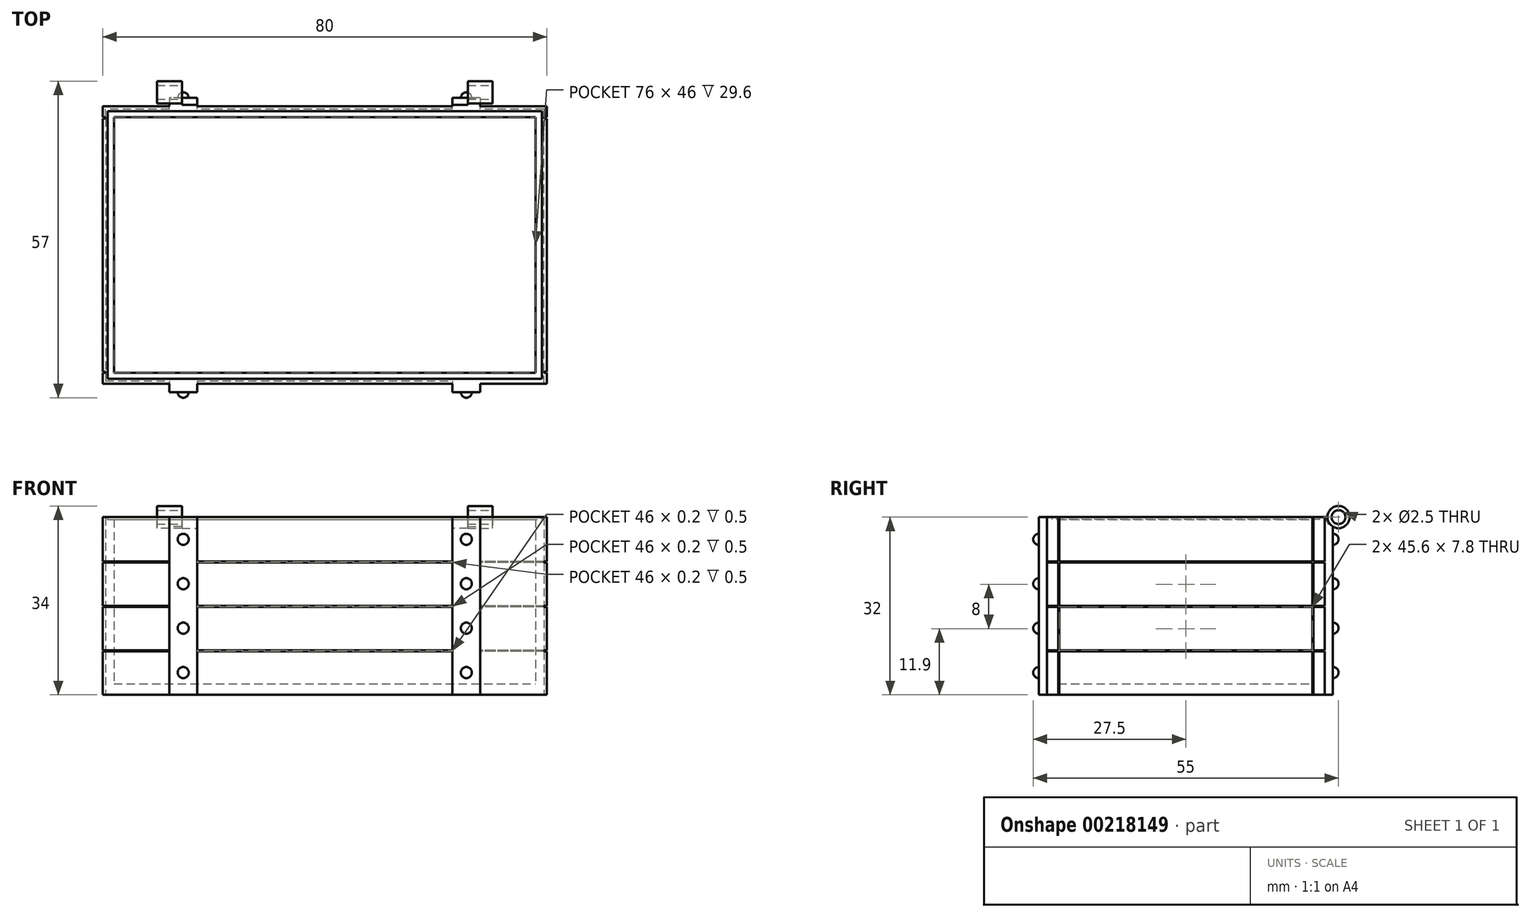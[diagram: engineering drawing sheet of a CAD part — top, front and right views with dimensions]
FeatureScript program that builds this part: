
annotation { "Feature Type Name" : "Feature", "Feature Type Description" : "" }
export const myFeature = defineFeature(function(context is Context, id is Id, definition is map)
    precondition{}
    {
        {
            var Q0;
            Q0=qCreatedBy(makeId("Top.planeOp"),FACE);
            var sketch = newSketch(context, id + "F0", { "sketchPlane" : qUnion([Q0])});
            skLineSegment(sketch, "E0.bottom", {"start": v(40, -25) * mm, "end": v(-40, -25) * mm});
            skLineSegment(sketch, "E0.top", {"start": v(40, 25) * mm, "end": v(-40, 25) * mm});
            skLineSegment(sketch, "E0.left", {"start": v(40, -25) * mm, "end": v(40, 25) * mm});
            skLineSegment(sketch, "E0.right", {"start": v(-40, -25) * mm, "end": v(-40, 25) * mm});
            skPoint(sketch, "E0.middle", {"position": v(0, 0) * mm});
            skSolve(sketch);
        }
        {
            var Q0;
            Q0 = qSketchRegion(id + "F0", true);
            extrude(context, id + "F1", {"entities" : qUnion([Q0]), "depth" : 2 * mm});
        }
        {
            var Q0;
            Q0=makeQuery(id+"F1.opExtrude","CAP_FACE",FACE,{"disambiguationData":[OSD([sQuery(id+"F0.wireOp",EDGE,"E0.bottom"),sQuery(id+"F0.wireOp",EDGE,"E0.top"),sQuery(id+"F0.wireOp",EDGE,"E0.left"),sQuery(id+"F0.wireOp",EDGE,"E0.right")])],"isStart":false});
            var sketch = newSketch(context, id + "F2", { "sketchPlane" : qUnion([Q0])});
            skLineSegment(sketch, "E1.bottom", {"start": v(40, -25) * mm, "end": v(-40, -25) * mm});
            skLineSegment(sketch, "E1.top", {"start": v(40, 25) * mm, "end": v(-40, 25) * mm});
            skLineSegment(sketch, "E1.left", {"start": v(40, -25) * mm, "end": v(40, 25) * mm});
            skLineSegment(sketch, "E1.right", {"start": v(-40, -25) * mm, "end": v(-40, 25) * mm});
            skPoint(sketch, "E1.middle", {"position": v(0, 0) * mm});
            skLineSegment(sketch, "E2.0", {"start": v(38, -23) * mm, "end": v(38, 23) * mm});
            skLineSegment(sketch, "E2.1", {"start": v(-38, -23) * mm, "end": v(38, -23) * mm});
            skLineSegment(sketch, "E2.2", {"start": v(-38, 23) * mm, "end": v(-38, -23) * mm});
            skLineSegment(sketch, "E2.3", {"start": v(38, 23) * mm, "end": v(-38, 23) * mm});
            skSolve(sketch);
        }
        {
            var Q0;
            Q0 = qSketchRegion(id + "F2", true);
            extrude(context, id + "F3", {"entities" : qUnion([Q0]), "operationType" : NewBodyOperationType.ADD, "depth" : 30 * mm});
        }
        {
            var Q0;
            Q0=makeQuery(id+"F3.boolean.opBoolean","MERGE",FACE,{"derivedFrom":[makeQuery(id+"F1.opExtrude","SWEPT_FACE",FACE,{"disambiguationData":[OSD([sQuery(id+"F0.wireOp",EDGE,"E0.top")])]}),makeQuery(id+"F3.opExtrude","SWEPT_FACE",FACE,{"disambiguationData":[OSD([sQuery(id+"F2.wireOp",EDGE,"E1.top")])]})]});
            var sketch = newSketch(context, id + "F4", { "sketchPlane" : qUnion([Q0])});
            skLineSegment(sketch, "E3.bottom", {"start": v(-28, 32) * mm, "end": v(-23, 32) * mm});
            skLineSegment(sketch, "E3.top", {"start": v(-28, 0) * mm, "end": v(-23, 0) * mm});
            skLineSegment(sketch, "E3.left", {"start": v(-28, 32) * mm, "end": v(-28, 0) * mm});
            skLineSegment(sketch, "E3.right", {"start": v(-23, 32) * mm, "end": v(-23, 0) * mm});
            skLineSegment(sketch, "E4.MirrorCS", {"start": v(23, 32) * mm, "end": v(23, 0) * mm});
            skLineSegment(sketch, "E5.MirrorCS", {"start": v(28, 32) * mm, "end": v(23, 32) * mm});
            skLineSegment(sketch, "E6.MirrorCS", {"start": v(28, 32) * mm, "end": v(28, 0) * mm});
            skLineSegment(sketch, "E7.MirrorCS", {"start": v(28, 0) * mm, "end": v(23, 0) * mm});
            skSolve(sketch);
        }
        {
            var Q0;
            Q0 = qSketchRegion(id + "F4", true);
            extrude(context, id + "F5", {"entities" : qUnion([Q0]), "operationType" : NewBodyOperationType.ADD, "depth" : 1.5 * mm});
        }
        {
            var Q0;
            Q0=makeQuery(id+"F5.opExtrude","SWEPT_FACE",FACE,{"disambiguationData":[OSD([sQuery(id+"F4.wireOp",EDGE,"E3.left")])]});
            var sketch = newSketch(context, id + "F6", { "sketchPlane" : qUnion([Q0])});
            skCircle(sketch, "E8", {"center": v(27.5, 32) * mm, "radius": 2 * mm});
            skSolve(sketch);
        }
        {
            var Q0;
            Q0 = qSketchRegion(id + "F6", true);
            extrude(context, id + "F7", {"entities" : qUnion([Q0]), "operationType" : NewBodyOperationType.ADD, "oppositeDirection" : true, "depth" : 4.5 * mm, "symmetric" : true});
        }
        {
            var Q0;
            Q0=makeQuery(id+"F5.opExtrude","SWEPT_FACE",FACE,{"disambiguationData":[OSD([sQuery(id+"F4.wireOp",EDGE,"E6.MirrorCS")])]});
            var sketch = newSketch(context, id + "F8", { "sketchPlane" : qUnion([Q0])});
            skCircle(sketch, "E9", {"center": v(-27.5, 32) * mm, "radius": 2 * mm});
            skSolve(sketch);
        }
        {
            var Q0;
            Q0 = qSketchRegion(id + "F8", true);
            extrude(context, id + "F9", {"entities" : qUnion([Q0]), "operationType" : NewBodyOperationType.ADD, "oppositeDirection" : true, "depth" : 4.5 * mm, "symmetric" : true});
        }
        {
            var Q0;
            Q0=qCreatedBy(makeId("Right.planeOp"),FACE);
            var sketch = newSketch(context, id + "F10", { "sketchPlane" : qUnion([Q0])});
            skCircle(sketch, "E10", {"center": v(27.5, 32) * mm, "radius": 1.25 * mm});
            skSolve(sketch);
        }
        {
            var Q0;
            Q0 = qSketchRegion(id + "F10", true);
            extrude(context, id + "F11", {"entities" : qUnion([Q0]), "operationType" : NewBodyOperationType.REMOVE, "oppositeDirection" : true, "depth" : 70 * mm, "symmetric" : true});
        }
        {
            var Q0;
            Q0=makeQuery(id+"F3.boolean.opBoolean","MERGE",FACE,{"derivedFrom":[makeQuery(id+"F1.opExtrude","SWEPT_FACE",FACE,{"disambiguationData":[OSD([sQuery(id+"F0.wireOp",EDGE,"E0.bottom")])]}),makeQuery(id+"F3.opExtrude","SWEPT_FACE",FACE,{"disambiguationData":[OSD([sQuery(id+"F2.wireOp",EDGE,"E1.bottom")])]})]});
            var sketch = newSketch(context, id + "F12", { "sketchPlane" : qUnion([Q0])});
            skLineSegment(sketch, "E11.bottom", {"start": v(-28, 0) * mm, "end": v(-23, 0) * mm});
            skLineSegment(sketch, "E11.top", {"start": v(-28, 32) * mm, "end": v(-23, 32) * mm});
            skLineSegment(sketch, "E11.left", {"start": v(-28, 0) * mm, "end": v(-28, 32) * mm});
            skLineSegment(sketch, "E11.right", {"start": v(-23, 0) * mm, "end": v(-23, 32) * mm});
            skLineSegment(sketch, "E12.bottom", {"start": v(23, 0) * mm, "end": v(28, 0) * mm});
            skLineSegment(sketch, "E12.top", {"start": v(23, 32) * mm, "end": v(28, 32) * mm});
            skLineSegment(sketch, "E12.left", {"start": v(23, 0) * mm, "end": v(23, 32) * mm});
            skLineSegment(sketch, "E12.right", {"start": v(28, 0) * mm, "end": v(28, 32) * mm});
            skSolve(sketch);
        }
        {
            var Q0;
            Q0 = qSketchRegion(id + "F12", true);
            extrude(context, id + "F13", {"entities" : qUnion([Q0]), "operationType" : NewBodyOperationType.ADD, "depth" : 1.5 * mm});
        }
        {
            var Q0;
            Q0=makeQuery(id+"F5.opExtrude","SWEPT_FACE",FACE,{"disambiguationData":[OSD([sQuery(id+"F4.wireOp",EDGE,"E4.MirrorCS")])]});
            var sketch = newSketch(context, id + "F14", { "sketchPlane" : qUnion([Q0])});
            skCircle(sketch, "E13", {"center": v(27.5, 32) * mm, "radius": 2.25 * mm});
            skSolve(sketch);
        }
        {
            var Q0;
            {var subQ1=sQuery(id+"F4.wireOp",EDGE,"E4.MirrorCS");var subQ6=makeQuery(id+"F11.boolean.opBoolean","INTERSECT",EDGE,{"derivedFrom":[makeQuery(id+"F5.opExtrude","SWEPT_FACE",FACE,{"disambiguationData":[OSD([subQ1])]}),makeQuery(id+"F11.opExtrude","SWEPT_FACE",FACE,{"disambiguationData":[OSD([sQuery(id+"F10.wireOp",EDGE,"E10")])]})]});Q0=makeQuery(id+"F14.imprint","IMPRINT",FACE,{"disambiguationData":[TD([[makeQuery(id+"F14.imprint","IMPRINT",EDGE,{"derivedFrom":subQ6}),1.0]])]});}
            var Q1;
            Q1=makeQuery(id+"F9.opExtrude","CAP_FACE",FACE,{"disambiguationData":[OSD([sQuery(id+"F8.wireOp",EDGE,"E9")])],"isStart":false});
            extrude(context, id + "F15", {"entities" : qUnion([Q0]), "operationType" : NewBodyOperationType.REMOVE, "endBound" : BoundingType.UP_TO_SURFACE, "oppositeDirection" : true, "endBoundEntityFace" : qUnion([Q1]), "depth" : 25 * mm});
        }
        {
            var Q0;
            Q0=makeQuery(id+"F5.opExtrude","SWEPT_FACE",FACE,{"disambiguationData":[OSD([sQuery(id+"F4.wireOp",EDGE,"E3.right")])]});
            var sketch = newSketch(context, id + "F16", { "sketchPlane" : qUnion([Q0])});
            skCircle(sketch, "E14", {"center": v(-27.5, 32) * mm, "radius": 2.25 * mm});
            skSolve(sketch);
        }
        {
            var Q0;
            {var subQ1=sQuery(id+"F4.wireOp",EDGE,"E3.right");var subQ6=makeQuery(id+"F11.boolean.opBoolean","INTERSECT",EDGE,{"derivedFrom":[makeQuery(id+"F5.opExtrude","SWEPT_FACE",FACE,{"disambiguationData":[OSD([subQ1])]}),makeQuery(id+"F11.opExtrude","SWEPT_FACE",FACE,{"disambiguationData":[OSD([sQuery(id+"F10.wireOp",EDGE,"E10")])]})]});Q0=makeQuery(id+"F16.imprint","IMPRINT",FACE,{"disambiguationData":[TD([[makeQuery(id+"F16.imprint","IMPRINT",EDGE,{"derivedFrom":subQ6}),-1.0]])]});}
            var Q1;
            Q1=makeQuery(id+"F7.opExtrude","CAP_FACE",FACE,{"disambiguationData":[OSD([sQuery(id+"F6.wireOp",EDGE,"E8")])],"isStart":false});
            extrude(context, id + "F17", {"entities" : qUnion([Q0]), "operationType" : NewBodyOperationType.REMOVE, "endBound" : BoundingType.UP_TO_SURFACE, "oppositeDirection" : true, "endBoundEntityFace" : qUnion([Q1]), "depth" : 25 * mm});
        }
        {
            var Q0;
            Q0=makeQuery(id+"F13.opExtrude","CAP_FACE",FACE,{"disambiguationData":[OSD([sQuery(id+"F12.wireOp",EDGE,"E11.bottom"),sQuery(id+"F12.wireOp",EDGE,"E11.top"),sQuery(id+"F12.wireOp",EDGE,"E11.left"),sQuery(id+"F12.wireOp",EDGE,"E11.right")])],"isStart":false});
            var sketch = newSketch(context, id + "F18", { "sketchPlane" : qUnion([Q0])});
            skLineSegment(sketch, "E15", {"start": v(-25.5, 32) * mm, "end": v(-25.5, 0) * mm, "construction": true});
            skCircle(sketch, "E16", {"center": v(-25.5, 28) * mm, "radius": 1 * mm});
            skCircle(sketch, "E17", {"center": v(-25.5, 20) * mm, "radius": 1 * mm});
            skCircle(sketch, "E18", {"center": v(-25.5, 12) * mm, "radius": 1 * mm});
            skCircle(sketch, "E19", {"center": v(-25.5, 4) * mm, "radius": 1 * mm});
            skSolve(sketch);
        }
        {
            var Q0;
            Q0=makeQuery(id+"F13.opExtrude","CAP_FACE",FACE,{"disambiguationData":[OSD([sQuery(id+"F12.wireOp",EDGE,"E12.bottom"),sQuery(id+"F12.wireOp",EDGE,"E12.top"),sQuery(id+"F12.wireOp",EDGE,"E12.left"),sQuery(id+"F12.wireOp",EDGE,"E12.right")])],"isStart":false});
            var sketch = newSketch(context, id + "F19", { "sketchPlane" : qUnion([Q0])});
            skLineSegment(sketch, "E20", {"start": v(25.5, 32) * mm, "end": v(25.5, 0) * mm, "construction": true});
            skCircle(sketch, "E21", {"center": v(25.5, 28) * mm, "radius": 1 * mm});
            skCircle(sketch, "E22", {"center": v(25.5, 20) * mm, "radius": 1 * mm});
            skCircle(sketch, "E23", {"center": v(25.5, 12) * mm, "radius": 1 * mm});
            skCircle(sketch, "E24", {"center": v(25.5, 4) * mm, "radius": 1 * mm});
            skSolve(sketch);
        }
        {
            var Q0;
            Q0=makeQuery(id+"F18.imprint","IMPRINT",FACE,{"disambiguationData":[TD([[makeQuery(id+"F18.imprint","IMPRINT",EDGE,{"derivedFrom":sQuery(id+"F18.wireOp",EDGE,"E16")}),1.0]])]});
            var Q1;
            Q1=makeQuery(id+"F18.imprint","IMPRINT",FACE,{"disambiguationData":[TD([[makeQuery(id+"F18.imprint","IMPRINT",EDGE,{"derivedFrom":sQuery(id+"F18.wireOp",EDGE,"E17")}),1.0]])]});
            var Q2;
            Q2=makeQuery(id+"F18.imprint","IMPRINT",FACE,{"disambiguationData":[TD([[makeQuery(id+"F18.imprint","IMPRINT",EDGE,{"derivedFrom":sQuery(id+"F18.wireOp",EDGE,"E18")}),1.0]])]});
            var Q3;
            Q3=makeQuery(id+"F18.imprint","IMPRINT",FACE,{"disambiguationData":[TD([[makeQuery(id+"F18.imprint","IMPRINT",EDGE,{"derivedFrom":sQuery(id+"F18.wireOp",EDGE,"E19")}),1.0]])]});
            var Q4;
            Q4=makeQuery(id+"F19.imprint","IMPRINT",FACE,{"disambiguationData":[TD([[makeQuery(id+"F19.imprint","IMPRINT",EDGE,{"derivedFrom":sQuery(id+"F19.wireOp",EDGE,"E21")}),1.0]])]});
            var Q5;
            Q5=makeQuery(id+"F19.imprint","IMPRINT",FACE,{"disambiguationData":[TD([[makeQuery(id+"F19.imprint","IMPRINT",EDGE,{"derivedFrom":sQuery(id+"F19.wireOp",EDGE,"E22")}),1.0]])]});
            var Q6;
            Q6=makeQuery(id+"F19.imprint","IMPRINT",FACE,{"disambiguationData":[TD([[makeQuery(id+"F19.imprint","IMPRINT",EDGE,{"derivedFrom":sQuery(id+"F19.wireOp",EDGE,"E23")}),1.0]])]});
            var Q7;
            Q7=makeQuery(id+"F19.imprint","IMPRINT",FACE,{"disambiguationData":[TD([[makeQuery(id+"F19.imprint","IMPRINT",EDGE,{"derivedFrom":sQuery(id+"F19.wireOp",EDGE,"E24")}),1.0]])]});
            extrude(context, id + "F20", {"entities" : qUnion([Q0, Q1, Q2, Q3, Q4, Q5, Q6, Q7]), "operationType" : NewBodyOperationType.ADD, "depth" : 1 * mm});
        }
        {
            var Q0;
            Q0=makeQuery(id+"F20.opExtrude","CAP_FACE",FACE,{"disambiguationData":[OSD([sQuery(id+"F18.wireOp",EDGE,"E16")])],"isStart":false});
            var Q1;
            Q1=makeQuery(id+"F20.opExtrude","CAP_FACE",FACE,{"disambiguationData":[OSD([sQuery(id+"F18.wireOp",EDGE,"E17")])],"isStart":false});
            var Q2;
            Q2=makeQuery(id+"F20.opExtrude","CAP_FACE",FACE,{"disambiguationData":[OSD([sQuery(id+"F18.wireOp",EDGE,"E18")])],"isStart":false});
            var Q3;
            Q3=makeQuery(id+"F20.opExtrude","CAP_FACE",FACE,{"disambiguationData":[OSD([sQuery(id+"F18.wireOp",EDGE,"E19")])],"isStart":false});
            var Q4;
            Q4=makeQuery(id+"F20.opExtrude","CAP_FACE",FACE,{"disambiguationData":[OSD([sQuery(id+"F19.wireOp",EDGE,"E21")])],"isStart":false});
            var Q5;
            Q5=makeQuery(id+"F20.opExtrude","CAP_FACE",FACE,{"disambiguationData":[OSD([sQuery(id+"F19.wireOp",EDGE,"E22")])],"isStart":false});
            var Q6;
            Q6=makeQuery(id+"F20.opExtrude","CAP_FACE",FACE,{"disambiguationData":[OSD([sQuery(id+"F19.wireOp",EDGE,"E23")])],"isStart":false});
            var Q7;
            Q7=makeQuery(id+"F20.opExtrude","CAP_EDGE",EDGE,{"disambiguationData":[OSD([sQuery(id+"F19.wireOp",EDGE,"E24")])],"isStart":false});
            fillet(context, id + "F21", {"entities" : qUnion([Q0, Q1, Q2, Q3, Q4, Q5, Q6, Q7]), "radius" : 1 * mm, "tangentPropagation" : true, "allowEdgeOverflow" : false});
        }
        {
            var Q0;
            Q0=makeQuery(id+"F5.opExtrude","CAP_FACE",FACE,{"disambiguationData":[OSD([sQuery(id+"F4.wireOp",EDGE,"E3.bottom"),sQuery(id+"F4.wireOp",EDGE,"E3.top"),sQuery(id+"F4.wireOp",EDGE,"E3.left"),sQuery(id+"F4.wireOp",EDGE,"E3.right")])],"isStart":false});
            var sketch = newSketch(context, id + "F22", { "sketchPlane" : qUnion([Q0])});
            skLineSegment(sketch, "E25", {"start": v(-25.5, 0) * mm, "end": v(-25.5, 29.98) * mm, "construction": true});
            skCircle(sketch, "E26", {"center": v(-25.5, 4) * mm, "radius": 1 * mm});
            skCircle(sketch, "E27", {"center": v(-25.5, 12) * mm, "radius": 1 * mm});
            skCircle(sketch, "E28", {"center": v(-25.5, 20) * mm, "radius": 1 * mm});
            skCircle(sketch, "E29", {"center": v(-25.5, 28) * mm, "radius": 1 * mm});
            skSolve(sketch);
        }
        {
            var Q0;
            Q0=makeQuery(id+"F5.opExtrude","CAP_FACE",FACE,{"disambiguationData":[OSD([sQuery(id+"F4.wireOp",EDGE,"E4.MirrorCS"),sQuery(id+"F4.wireOp",EDGE,"E5.MirrorCS"),sQuery(id+"F4.wireOp",EDGE,"E6.MirrorCS"),sQuery(id+"F4.wireOp",EDGE,"E7.MirrorCS")])],"isStart":false});
            var sketch = newSketch(context, id + "F23", { "sketchPlane" : qUnion([Q0])});
            skLineSegment(sketch, "E30", {"start": v(25.5, 0) * mm, "end": v(25.5, 29.98) * mm, "construction": true});
            skCircle(sketch, "E31", {"center": v(25.5, 4) * mm, "radius": 1 * mm});
            skCircle(sketch, "E32", {"center": v(25.5, 12) * mm, "radius": 1 * mm});
            skCircle(sketch, "E33", {"center": v(25.5, 20) * mm, "radius": 1 * mm});
            skCircle(sketch, "E34", {"center": v(25.5, 28) * mm, "radius": 1 * mm});
            skSolve(sketch);
        }
        {
            var Q0;
            Q0=makeQuery(id+"F22.imprint","IMPRINT",FACE,{"disambiguationData":[TD([[makeQuery(id+"F22.imprint","IMPRINT",EDGE,{"derivedFrom":sQuery(id+"F22.wireOp",EDGE,"E29")}),1.0]])]});
            var Q1;
            Q1=makeQuery(id+"F22.imprint","IMPRINT",FACE,{"disambiguationData":[TD([[makeQuery(id+"F22.imprint","IMPRINT",EDGE,{"derivedFrom":sQuery(id+"F22.wireOp",EDGE,"E28")}),1.0]])]});
            var Q2;
            Q2=makeQuery(id+"F22.imprint","IMPRINT",FACE,{"disambiguationData":[TD([[makeQuery(id+"F22.imprint","IMPRINT",EDGE,{"derivedFrom":sQuery(id+"F22.wireOp",EDGE,"E27")}),1.0]])]});
            var Q3;
            Q3=makeQuery(id+"F22.imprint","IMPRINT",FACE,{"disambiguationData":[TD([[makeQuery(id+"F22.imprint","IMPRINT",EDGE,{"derivedFrom":sQuery(id+"F22.wireOp",EDGE,"E26")}),1.0]])]});
            var Q4;
            Q4=makeQuery(id+"F23.imprint","IMPRINT",FACE,{"disambiguationData":[TD([[makeQuery(id+"F23.imprint","IMPRINT",EDGE,{"derivedFrom":sQuery(id+"F23.wireOp",EDGE,"E34")}),1.0]])]});
            var Q5;
            Q5=makeQuery(id+"F23.imprint","IMPRINT",FACE,{"disambiguationData":[TD([[makeQuery(id+"F23.imprint","IMPRINT",EDGE,{"derivedFrom":sQuery(id+"F23.wireOp",EDGE,"E33")}),1.0]])]});
            var Q6;
            Q6=makeQuery(id+"F23.imprint","IMPRINT",FACE,{"disambiguationData":[TD([[makeQuery(id+"F23.imprint","IMPRINT",EDGE,{"derivedFrom":sQuery(id+"F23.wireOp",EDGE,"E32")}),1.0]])]});
            var Q7;
            Q7=makeQuery(id+"F23.imprint","IMPRINT",FACE,{"disambiguationData":[TD([[makeQuery(id+"F23.imprint","IMPRINT",EDGE,{"derivedFrom":sQuery(id+"F23.wireOp",EDGE,"E31")}),1.0]])]});
            extrude(context, id + "F24", {"entities" : qUnion([Q0, Q1, Q2, Q3, Q4, Q5, Q6, Q7]), "operationType" : NewBodyOperationType.ADD, "depth" : 1 * mm});
        }
        {
            var Q0;
            Q0=makeQuery(id+"F24.opExtrude","CAP_FACE",FACE,{"disambiguationData":[OSD([sQuery(id+"F22.wireOp",EDGE,"E29")])],"isStart":false});
            var Q1;
            Q1=makeQuery(id+"F24.opExtrude","CAP_EDGE",EDGE,{"disambiguationData":[OSD([sQuery(id+"F22.wireOp",EDGE,"E28")])],"isStart":false});
            var Q2;
            Q2=makeQuery(id+"F24.opExtrude","CAP_EDGE",EDGE,{"disambiguationData":[OSD([sQuery(id+"F22.wireOp",EDGE,"E27")])],"isStart":false});
            var Q3;
            Q3=makeQuery(id+"F24.opExtrude","CAP_EDGE",EDGE,{"disambiguationData":[OSD([sQuery(id+"F22.wireOp",EDGE,"E26")])],"isStart":false});
            var Q4;
            Q4=makeQuery(id+"F24.opExtrude","CAP_FACE",FACE,{"disambiguationData":[OSD([sQuery(id+"F23.wireOp",EDGE,"E34")])],"isStart":false});
            var Q5;
            Q5=makeQuery(id+"F24.opExtrude","CAP_FACE",FACE,{"disambiguationData":[OSD([sQuery(id+"F23.wireOp",EDGE,"E33")])],"isStart":false});
            var Q6;
            Q6=makeQuery(id+"F24.opExtrude","CAP_EDGE",EDGE,{"disambiguationData":[OSD([sQuery(id+"F23.wireOp",EDGE,"E32")])],"isStart":false});
            var Q7;
            Q7=makeQuery(id+"F24.opExtrude","CAP_EDGE",EDGE,{"disambiguationData":[OSD([sQuery(id+"F23.wireOp",EDGE,"E31")])],"isStart":false});
            fillet(context, id + "F25", {"entities" : qUnion([Q0, Q1, Q2, Q3, Q4, Q5, Q6, Q7]), "radius" : 1 * mm, "tangentPropagation" : true, "allowEdgeOverflow" : false});
        }
        {
            var Q0;
            {var subQ0=sQuery(id+"F0.wireOp",EDGE,"E0.bottom");var subQ1=sQuery(id+"F2.wireOp",EDGE,"E1.bottom");Q0=makeQuery(id+"F13.boolean.opBoolean","SPLIT",FACE,{"disambiguationData":[TD([makeQuery(id+"F13.opExtrude","SWEPT_FACE",FACE,{"disambiguationData":[OSD([sQuery(id+"F12.wireOp",EDGE,"E11.right")])]})])],"derivedFrom":makeQuery(id+"F3.boolean.opBoolean","MERGE",FACE,{"derivedFrom":[makeQuery(id+"F1.opExtrude","SWEPT_FACE",FACE,{"disambiguationData":[OSD([subQ0])]}),makeQuery(id+"F3.opExtrude","SWEPT_FACE",FACE,{"disambiguationData":[OSD([subQ1])]})]})});}
            var sketch = newSketch(context, id + "F26", { "sketchPlane" : qUnion([Q0])});
            skLineSegment(sketch, "E35.bottom", {"start": v(-40, 0) * mm, "end": v(40, 0) * mm});
            skLineSegment(sketch, "E35.top", {"start": v(-40, 32) * mm, "end": v(40, 32) * mm});
            skLineSegment(sketch, "E35.left", {"start": v(-40, 0) * mm, "end": v(-40, 32) * mm});
            skLineSegment(sketch, "E35.right", {"start": v(40, 0) * mm, "end": v(40, 32) * mm});
            skLineSegment(sketch, "E36", {"start": v(-40, 24) * mm, "end": v(-28, 24) * mm});
            skLineSegment(sketch, "E37", {"start": v(-40, 16) * mm, "end": v(-28, 16) * mm});
            skLineSegment(sketch, "E38", {"start": v(-40, 8) * mm, "end": v(-28, 8) * mm});
            skLineSegment(sketch, "E39", {"start": v(-40, 23.8) * mm, "end": v(-28, 23.8) * mm});
            skLineSegment(sketch, "E40", {"start": v(-40, 15.8) * mm, "end": v(-28, 15.8) * mm});
            skLineSegment(sketch, "E41", {"start": v(-40, 7.8) * mm, "end": v(-28, 7.8) * mm});
            skLineSegment(sketch, "E42", {"start": v(-40, 24) * mm, "end": v(-40, 23.8) * mm});
            skLineSegment(sketch, "E43", {"start": v(-40, 16) * mm, "end": v(-40, 15.8) * mm});
            skLineSegment(sketch, "E44", {"start": v(-40, 8) * mm, "end": v(-40, 7.8) * mm});
            skLineSegment(sketch, "E45", {"start": v(40, 24) * mm, "end": v(40, 23.8) * mm});
            skLineSegment(sketch, "E46", {"start": v(40, 15.8) * mm, "end": v(40, 16) * mm});
            skLineSegment(sketch, "E47", {"start": v(40, 7.8) * mm, "end": v(40, 8) * mm});
            skLineSegment(sketch, "E48", {"start": v(-28, 23.8) * mm, "end": v(-28, 24) * mm});
            skLineSegment(sketch, "E49", {"start": v(-28, 15.8) * mm, "end": v(-28, 16) * mm});
            skLineSegment(sketch, "E50", {"start": v(-28, 8) * mm, "end": v(-28, 7.8) * mm});
            skLineSegment(sketch, "E51", {"start": v(-23, 24) * mm, "end": v(-23, 23.8) * mm});
            skLineSegment(sketch, "E52", {"start": v(-23, 16) * mm, "end": v(-23, 15.8) * mm});
            skLineSegment(sketch, "E53", {"start": v(-23, 8) * mm, "end": v(-23, 7.8) * mm});
            skLineSegment(sketch, "E54", {"start": v(23, 24) * mm, "end": v(23, 23.8) * mm});
            skLineSegment(sketch, "E55", {"start": v(28, 24) * mm, "end": v(28, 23.8) * mm});
            skLineSegment(sketch, "E56", {"start": v(23, 16) * mm, "end": v(23, 15.8) * mm});
            skLineSegment(sketch, "E57", {"start": v(28, 16) * mm, "end": v(28, 15.8) * mm});
            skLineSegment(sketch, "E58", {"start": v(23, 8) * mm, "end": v(23, 7.8) * mm});
            skLineSegment(sketch, "E59", {"start": v(28, 8) * mm, "end": v(28, 7.8) * mm});
            skLineSegment(sketch, "E60.trimOffspring", {"start": v(-23, 24) * mm, "end": v(23, 24) * mm});
            skLineSegment(sketch, "E61.trimOffspring", {"start": v(-23, 23.8) * mm, "end": v(23, 23.8) * mm});
            skLineSegment(sketch, "E62.trimOffspring", {"start": v(-23, 16) * mm, "end": v(23, 16) * mm});
            skLineSegment(sketch, "E63.trimOffspring", {"start": v(-23, 15.8) * mm, "end": v(23, 15.8) * mm});
            skLineSegment(sketch, "E64.trimOffspring", {"start": v(-23, 8) * mm, "end": v(23, 8) * mm});
            skLineSegment(sketch, "E65.trimOffspring", {"start": v(-23, 7.8) * mm, "end": v(23, 7.8) * mm});
            skLineSegment(sketch, "E66.trimOffspring", {"start": v(28, 8) * mm, "end": v(40, 8) * mm});
            skLineSegment(sketch, "E67.trimOffspring", {"start": v(28, 7.8) * mm, "end": v(40, 7.8) * mm});
            skLineSegment(sketch, "E68.trimOffspring", {"start": v(28, 15.8) * mm, "end": v(40, 15.8) * mm});
            skLineSegment(sketch, "E69.trimOffspring", {"start": v(28, 16) * mm, "end": v(40, 16) * mm});
            skLineSegment(sketch, "E70.trimOffspring", {"start": v(28, 23.8) * mm, "end": v(40, 23.8) * mm});
            skLineSegment(sketch, "E71.trimOffspring", {"start": v(28, 24) * mm, "end": v(40, 24) * mm});
            skSolve(sketch);
        }
        {
            var Q0;
            Q0=makeQuery(id+"F26.imprint","IMPRINT",FACE,{"disambiguationData":[TD([[makeQuery(id+"F26.imprint","IMPRINT",EDGE,{"derivedFrom":sQuery(id+"F26.wireOp",EDGE,"E36")}),-1.0]])]});
            var Q1;
            Q1=makeQuery(id+"F26.imprint","IMPRINT",FACE,{"disambiguationData":[TD([[makeQuery(id+"F26.imprint","IMPRINT",EDGE,{"derivedFrom":sQuery(id+"F26.wireOp",EDGE,"E37")}),-1.0]])]});
            var Q2;
            Q2=makeQuery(id+"F26.imprint","IMPRINT",FACE,{"disambiguationData":[TD([[makeQuery(id+"F26.imprint","IMPRINT",EDGE,{"derivedFrom":sQuery(id+"F26.wireOp",EDGE,"E38")}),-1.0]])]});
            var Q3;
            Q3=makeQuery(id+"F26.imprint","IMPRINT",FACE,{"disambiguationData":[TD([[makeQuery(id+"F26.imprint","IMPRINT",EDGE,{"derivedFrom":sQuery(id+"F26.wireOp",EDGE,"E53")}),-1.0]])]});
            var Q4;
            Q4=makeQuery(id+"F26.imprint","IMPRINT",FACE,{"disambiguationData":[TD([[makeQuery(id+"F26.imprint","IMPRINT",EDGE,{"derivedFrom":sQuery(id+"F26.wireOp",EDGE,"E52")}),-1.0]])]});
            var Q5;
            Q5=makeQuery(id+"F26.imprint","IMPRINT",FACE,{"disambiguationData":[TD([[makeQuery(id+"F26.imprint","IMPRINT",EDGE,{"derivedFrom":sQuery(id+"F26.wireOp",EDGE,"E51")}),-1.0]])]});
            var Q6;
            Q6=makeQuery(id+"F26.imprint","IMPRINT",FACE,{"disambiguationData":[TD([[makeQuery(id+"F26.imprint","IMPRINT",EDGE,{"derivedFrom":sQuery(id+"F26.wireOp",EDGE,"E45")}),-1.0]])]});
            var Q7;
            Q7=makeQuery(id+"F26.imprint","IMPRINT",FACE,{"disambiguationData":[TD([[makeQuery(id+"F26.imprint","IMPRINT",EDGE,{"derivedFrom":sQuery(id+"F26.wireOp",EDGE,"E46")}),1.0]])]});
            var Q8;
            Q8=makeQuery(id+"F26.imprint","IMPRINT",FACE,{"disambiguationData":[TD([[makeQuery(id+"F26.imprint","IMPRINT",EDGE,{"derivedFrom":sQuery(id+"F26.wireOp",EDGE,"E47")}),1.0]])]});
            extrude(context, id + "F27", {"entities" : qUnion([Q0, Q1, Q2, Q3, Q4, Q5, Q6, Q7, Q8]), "operationType" : NewBodyOperationType.REMOVE, "oppositeDirection" : true, "depth" : .5 * mm});
        }
        {
            var Q0;
            {var subQ0=sQuery(id+"F4.wireOp",EDGE,"E3.right");Q0=makeQuery(id+"F4.imprint","IMPRINT",FACE,{"disambiguationData":[TD([[makeQuery(id+"F4.imprint","IMPRINT",EDGE,{"derivedFrom":subQ0}),1.0]])]});}
            var sketch = newSketch(context, id + "F28", { "sketchPlane" : qUnion([Q0])});
            skLineSegment(sketch, "E72.bottom", {"start": v(-40, 24) * mm, "end": v(-28, 24) * mm});
            skLineSegment(sketch, "E72.top", {"start": v(-40, 23.8) * mm, "end": v(-28, 23.8) * mm});
            skLineSegment(sketch, "E72.left", {"start": v(-40, 24) * mm, "end": v(-40, 23.8) * mm});
            skLineSegment(sketch, "E72.right", {"start": v(-28, 24) * mm, "end": v(-28, 23.8) * mm});
            skLineSegment(sketch, "E73.bottom", {"start": v(-40, 16) * mm, "end": v(-28, 16) * mm});
            skLineSegment(sketch, "E73.top", {"start": v(-40, 15.8) * mm, "end": v(-28, 15.8) * mm});
            skLineSegment(sketch, "E73.left", {"start": v(-40, 16) * mm, "end": v(-40, 15.8) * mm});
            skLineSegment(sketch, "E73.right", {"start": v(-28, 16) * mm, "end": v(-28, 15.8) * mm});
            skLineSegment(sketch, "E74.bottom", {"start": v(-40, 8) * mm, "end": v(-28, 8) * mm});
            skLineSegment(sketch, "E74.top", {"start": v(-40, 7.8) * mm, "end": v(-28, 7.8) * mm});
            skLineSegment(sketch, "E74.left", {"start": v(-40, 8) * mm, "end": v(-40, 7.8) * mm});
            skLineSegment(sketch, "E74.right", {"start": v(-28, 8) * mm, "end": v(-28, 7.8) * mm});
            skLineSegment(sketch, "E75.bottom", {"start": v(-23, 24) * mm, "end": v(23, 24) * mm});
            skLineSegment(sketch, "E75.top", {"start": v(-23, 23.8) * mm, "end": v(23, 23.8) * mm});
            skLineSegment(sketch, "E75.left", {"start": v(-23, 24) * mm, "end": v(-23, 23.8) * mm});
            skLineSegment(sketch, "E75.right", {"start": v(23, 24) * mm, "end": v(23, 23.8) * mm});
            skLineSegment(sketch, "E76.bottom", {"start": v(-23, 16) * mm, "end": v(23, 16) * mm});
            skLineSegment(sketch, "E76.top", {"start": v(-23, 15.8) * mm, "end": v(23, 15.8) * mm});
            skLineSegment(sketch, "E76.left", {"start": v(-23, 16) * mm, "end": v(-23, 15.8) * mm});
            skLineSegment(sketch, "E76.right", {"start": v(23, 16) * mm, "end": v(23, 15.8) * mm});
            skLineSegment(sketch, "E77.bottom", {"start": v(-23, 8) * mm, "end": v(23, 8) * mm});
            skLineSegment(sketch, "E77.top", {"start": v(-23, 7.8) * mm, "end": v(23, 7.8) * mm});
            skLineSegment(sketch, "E77.left", {"start": v(-23, 8) * mm, "end": v(-23, 7.8) * mm});
            skLineSegment(sketch, "E77.right", {"start": v(23, 8) * mm, "end": v(23, 7.8) * mm});
            skLineSegment(sketch, "E78.bottom", {"start": v(28, 24) * mm, "end": v(40, 24) * mm});
            skLineSegment(sketch, "E78.top", {"start": v(28, 23.8) * mm, "end": v(40, 23.8) * mm});
            skLineSegment(sketch, "E78.left", {"start": v(28, 24) * mm, "end": v(28, 23.8) * mm});
            skLineSegment(sketch, "E78.right", {"start": v(40, 24) * mm, "end": v(40, 23.8) * mm});
            skLineSegment(sketch, "E79.bottom", {"start": v(28, 16) * mm, "end": v(40, 16) * mm});
            skLineSegment(sketch, "E79.top", {"start": v(28, 15.8) * mm, "end": v(40, 15.8) * mm});
            skLineSegment(sketch, "E79.left", {"start": v(28, 16) * mm, "end": v(28, 15.8) * mm});
            skLineSegment(sketch, "E79.right", {"start": v(40, 16) * mm, "end": v(40, 15.8) * mm});
            skLineSegment(sketch, "E80.bottom", {"start": v(28, 8) * mm, "end": v(40, 8) * mm});
            skLineSegment(sketch, "E80.top", {"start": v(28, 7.8) * mm, "end": v(40, 7.8) * mm});
            skLineSegment(sketch, "E80.left", {"start": v(28, 8) * mm, "end": v(28, 7.8) * mm});
            skLineSegment(sketch, "E80.right", {"start": v(40, 8) * mm, "end": v(40, 7.8) * mm});
            skSolve(sketch);
        }
        {
            var Q0;
            Q0 = qSketchRegion(id + "F28", true);
            extrude(context, id + "F29", {"entities" : qUnion([Q0]), "operationType" : NewBodyOperationType.REMOVE, "oppositeDirection" : true, "depth" : .5 * mm});
        }
        {
            var Q0;
            Q0=makeQuery(id+"F3.boolean.opBoolean","MERGE",FACE,{"derivedFrom":[makeQuery(id+"F1.opExtrude","SWEPT_FACE",FACE,{"disambiguationData":[OSD([sQuery(id+"F0.wireOp",EDGE,"E0.left")])]}),makeQuery(id+"F3.opExtrude","SWEPT_FACE",FACE,{"disambiguationData":[OSD([sQuery(id+"F2.wireOp",EDGE,"E1.left")])]})]});
            var sketch = newSketch(context, id + "F30", { "sketchPlane" : qUnion([Q0])});
            skLineSegment(sketch, "E81.bottom", {"start": v(-23, 32) * mm, "end": v(-22.8, 32) * mm});
            skLineSegment(sketch, "E81.top", {"start": v(-23, 0) * mm, "end": v(-22.8, 0) * mm});
            skLineSegment(sketch, "E81.left", {"start": v(-23, 32) * mm, "end": v(-23, 0) * mm});
            skLineSegment(sketch, "E81.right", {"start": v(-22.8, 32) * mm, "end": v(-22.8, 0) * mm});
            skLineSegment(sketch, "E82.bottom", {"start": v(22.8, 32) * mm, "end": v(23, 32) * mm});
            skLineSegment(sketch, "E82.top", {"start": v(22.8, 0) * mm, "end": v(23, 0) * mm});
            skLineSegment(sketch, "E82.left", {"start": v(22.8, 32) * mm, "end": v(22.8, 0) * mm});
            skLineSegment(sketch, "E82.right", {"start": v(23, 32) * mm, "end": v(23, 0) * mm});
            skLineSegment(sketch, "E83.bottom", {"start": v(-25, 24) * mm, "end": v(25, 24) * mm});
            skLineSegment(sketch, "E83.top", {"start": v(-25, 23.8) * mm, "end": v(25, 23.8) * mm});
            skLineSegment(sketch, "E83.left", {"start": v(-25, 24) * mm, "end": v(-25, 23.8) * mm});
            skLineSegment(sketch, "E83.right", {"start": v(25, 24) * mm, "end": v(25, 23.8) * mm});
            skLineSegment(sketch, "E84.bottom", {"start": v(-25, 16) * mm, "end": v(25, 16) * mm});
            skLineSegment(sketch, "E84.top", {"start": v(-25, 15.8) * mm, "end": v(25, 15.8) * mm});
            skLineSegment(sketch, "E84.left", {"start": v(-25, 16) * mm, "end": v(-25, 15.8) * mm});
            skLineSegment(sketch, "E84.right", {"start": v(25, 16) * mm, "end": v(25, 15.8) * mm});
            skLineSegment(sketch, "E85.bottom", {"start": v(-25, 8) * mm, "end": v(25, 8) * mm});
            skLineSegment(sketch, "E85.top", {"start": v(-25, 7.8) * mm, "end": v(25, 7.8) * mm});
            skLineSegment(sketch, "E85.left", {"start": v(-25, 8) * mm, "end": v(-25, 7.8) * mm});
            skLineSegment(sketch, "E85.right", {"start": v(25, 8) * mm, "end": v(25, 7.8) * mm});
            skSolve(sketch);
        }
        {
            var Q0;
            Q0 = qSketchRegion(id + "F30", true);
            var Q1;
            {var subQ0=sQuery(id+"F30.wireOp",EDGE,"E84.bottom");var subQ1=sQuery(id+"F30.wireOp",EDGE,"E81.right");var subQ2=makeQuery(id+"F30.imprint","INTERSECT",VERTEX,{"derivedFrom":[subQ1,subQ0]});Q1=makeQuery(id+"F30.imprint","IMPRINT",FACE,{"disambiguationData":[TD([[makeQuery(id+"F30.imprint","IMPRINT",EDGE,{"disambiguationData":[TD([[subQ2,-1.0]])],"derivedFrom":subQ1}),1.0]])]});}
            extrude(context, id + "F31", {"entities" : qUnion([Q0, Q1]), "operationType" : NewBodyOperationType.REMOVE, "oppositeDirection" : true, "depth" : .5 * mm});
        }
        {
            var Q0;
            Q0=makeQuery(id+"F3.boolean.opBoolean","MERGE",FACE,{"derivedFrom":[makeQuery(id+"F1.opExtrude","SWEPT_FACE",FACE,{"disambiguationData":[OSD([sQuery(id+"F0.wireOp",EDGE,"E0.right")])]}),makeQuery(id+"F3.opExtrude","SWEPT_FACE",FACE,{"disambiguationData":[OSD([sQuery(id+"F2.wireOp",EDGE,"E1.right")])]})]});
            var sketch = newSketch(context, id + "F32", { "sketchPlane" : qUnion([Q0])});
            skLineSegment(sketch, "E86.bottom", {"start": v(-23, 32) * mm, "end": v(-22.8, 32) * mm});
            skLineSegment(sketch, "E86.top", {"start": v(-23, 0) * mm, "end": v(-22.8, 0) * mm});
            skLineSegment(sketch, "E86.left", {"start": v(-23, 32) * mm, "end": v(-23, 0) * mm});
            skLineSegment(sketch, "E86.right", {"start": v(-22.8, 32) * mm, "end": v(-22.8, 0) * mm});
            skLineSegment(sketch, "E87.bottom", {"start": v(22.8, 32) * mm, "end": v(23, 32) * mm});
            skLineSegment(sketch, "E87.top", {"start": v(22.8, 0) * mm, "end": v(23, 0) * mm});
            skLineSegment(sketch, "E87.left", {"start": v(22.8, 32) * mm, "end": v(22.8, 0) * mm});
            skLineSegment(sketch, "E87.right", {"start": v(23, 32) * mm, "end": v(23, 0) * mm});
            skLineSegment(sketch, "E88.bottom", {"start": v(-25, 24) * mm, "end": v(25, 24) * mm});
            skLineSegment(sketch, "E88.top", {"start": v(-25, 23.8) * mm, "end": v(25, 23.8) * mm});
            skLineSegment(sketch, "E88.left", {"start": v(-25, 24) * mm, "end": v(-25, 23.8) * mm});
            skLineSegment(sketch, "E88.right", {"start": v(25, 24) * mm, "end": v(25, 23.8) * mm});
            skLineSegment(sketch, "E89.bottom", {"start": v(-25, 16) * mm, "end": v(25, 16) * mm});
            skLineSegment(sketch, "E89.top", {"start": v(-25, 15.8) * mm, "end": v(25, 15.8) * mm});
            skLineSegment(sketch, "E89.left", {"start": v(-25, 16) * mm, "end": v(-25, 15.8) * mm});
            skLineSegment(sketch, "E89.right", {"start": v(25, 16) * mm, "end": v(25, 15.8) * mm});
            skLineSegment(sketch, "E90.bottom", {"start": v(-25, 8) * mm, "end": v(25, 8) * mm});
            skLineSegment(sketch, "E90.top", {"start": v(-25, 7.8) * mm, "end": v(25, 7.8) * mm});
            skLineSegment(sketch, "E90.left", {"start": v(-25, 8) * mm, "end": v(-25, 7.8) * mm});
            skLineSegment(sketch, "E90.right", {"start": v(25, 8) * mm, "end": v(25, 7.8) * mm});
            skSolve(sketch);
        }
        {
            var Q0;
            Q0 = qSketchRegion(id + "F32", true);
            var Q1;
            {var subQ0=sQuery(id+"F32.wireOp",EDGE,"E89.bottom");var subQ1=sQuery(id+"F32.wireOp",EDGE,"E86.right");var subQ2=makeQuery(id+"F32.imprint","INTERSECT",VERTEX,{"derivedFrom":[subQ1,subQ0]});Q1=makeQuery(id+"F32.imprint","IMPRINT",FACE,{"disambiguationData":[TD([[makeQuery(id+"F32.imprint","IMPRINT",EDGE,{"disambiguationData":[TD([[subQ2,-1.0]])],"derivedFrom":subQ1}),1.0]])]});}
            extrude(context, id + "F33", {"entities" : qUnion([Q0, Q1]), "operationType" : NewBodyOperationType.REMOVE, "oppositeDirection" : true, "depth" : .5 * mm});
        }
        {
            var Q0;
            Q0=makeQuery(id+"F13.boolean.opBoolean","MERGE",FACE,{"derivedFrom":[makeQuery(id+"F5.boolean.opBoolean","MERGE",FACE,{"derivedFrom":[makeQuery(id+"F3.opExtrude","CAP_FACE",FACE,{"disambiguationData":[OSD([sQuery(id+"F2.wireOp",EDGE,"E1.bottom"),sQuery(id+"F2.wireOp",EDGE,"E1.top"),sQuery(id+"F2.wireOp",EDGE,"E1.left"),sQuery(id+"F2.wireOp",EDGE,"E1.right"),sQuery(id+"F2.wireOp",EDGE,"E2.0"),sQuery(id+"F2.wireOp",EDGE,"E2.1"),sQuery(id+"F2.wireOp",EDGE,"E2.2"),sQuery(id+"F2.wireOp",EDGE,"E2.3")])],"isStart":false}),makeQuery(id+"F5.opExtrude","SWEPT_FACE",FACE,{"disambiguationData":[OSD([sQuery(id+"F4.wireOp",EDGE,"E3.bottom")])]}),makeQuery(id+"F5.opExtrude","SWEPT_FACE",FACE,{"disambiguationData":[OSD([sQuery(id+"F4.wireOp",EDGE,"E5.MirrorCS")])]})]}),makeQuery(id+"F13.opExtrude","SWEPT_FACE",FACE,{"disambiguationData":[OSD([sQuery(id+"F12.wireOp",EDGE,"E11.top")])]}),makeQuery(id+"F13.opExtrude","SWEPT_FACE",FACE,{"disambiguationData":[OSD([sQuery(id+"F12.wireOp",EDGE,"E12.top")])]})]});
            var sketch = newSketch(context, id + "F34", { "sketchPlane" : qUnion([Q0])});
            skLineSegment(sketch, "E91.bottom", {"start": v(-40, 25) * mm, "end": v(40, 25) * mm});
            skLineSegment(sketch, "E91.top", {"start": v(-40, -25) * mm, "end": v(40, -25) * mm});
            skLineSegment(sketch, "E91.left", {"start": v(-40, 25) * mm, "end": v(-40, -25) * mm});
            skLineSegment(sketch, "E91.right", {"start": v(40, 25) * mm, "end": v(40, -25) * mm});
            skLineSegment(sketch, "E92.bottom", {"start": v(-28, -26.5) * mm, "end": v(-23, -26.5) * mm});
            skLineSegment(sketch, "E92.top", {"start": v(-28, -25) * mm, "end": v(-23, -25) * mm});
            skLineSegment(sketch, "E92.left", {"start": v(-28, -26.5) * mm, "end": v(-28, -25) * mm});
            skLineSegment(sketch, "E92.right", {"start": v(-23, -26.5) * mm, "end": v(-23, -25) * mm});
            skLineSegment(sketch, "E93.bottom", {"start": v(23, -25) * mm, "end": v(28, -25) * mm});
            skLineSegment(sketch, "E93.top", {"start": v(23, -26.5) * mm, "end": v(28, -26.5) * mm});
            skLineSegment(sketch, "E93.left", {"start": v(23, -25) * mm, "end": v(23, -26.5) * mm});
            skLineSegment(sketch, "E93.right", {"start": v(28, -25) * mm, "end": v(28, -26.5) * mm});
            skLineSegment(sketch, "E94.bottom", {"start": v(-39.1, 24.1) * mm, "end": v(39.1, 24.1) * mm});
            skLineSegment(sketch, "E94.top", {"start": v(-39.1, -24.1) * mm, "end": v(39.1, -24.1) * mm});
            skLineSegment(sketch, "E94.left", {"start": v(-39.1, 24.1) * mm, "end": v(-39.1, -24.1) * mm});
            skLineSegment(sketch, "E94.right", {"start": v(39.1, 24.1) * mm, "end": v(39.1, -24.1) * mm});
            skSolve(sketch);
        }
        {
            var Q0;
            Q0=makeQuery(id+"F34.imprint","IMPRINT",FACE,{"disambiguationData":[TD([[makeQuery(id+"F34.imprint","IMPRINT",EDGE,{"derivedFrom":sQuery(id+"F34.wireOp",EDGE,"E94.bottom")}),-1.0]])]});
            extrude(context, id + "F35", {"entities" : qUnion([Q0]), "operationType" : NewBodyOperationType.REMOVE, "oppositeDirection" : true, "depth" : 0.4 * mm});
        }
    });
